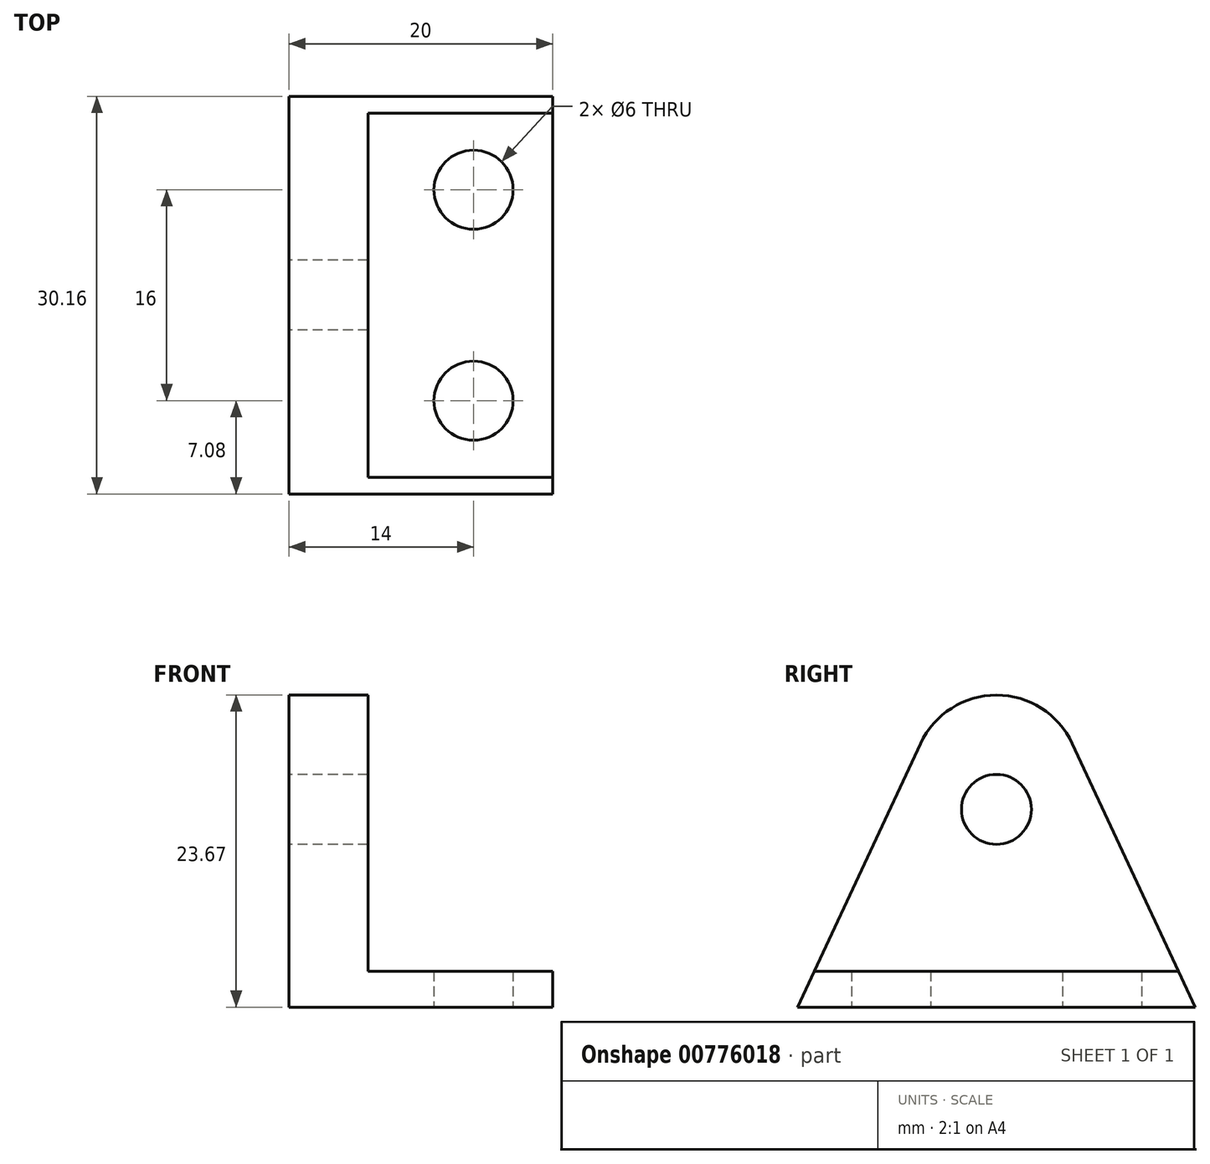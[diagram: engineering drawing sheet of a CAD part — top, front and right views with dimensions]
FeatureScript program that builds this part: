
annotation { "Feature Type Name" : "Feature", "Feature Type Description" : "" }
export const myFeature = defineFeature(function(context is Context, id is Id, definition is map)
    precondition{}
    {
        {
            var Q0;
            Q0=qCreatedBy(makeId("Right.planeOp"),FACE);
            var sketch = newSketch(context, id + "F0", { "sketchPlane" : qUnion([Q0])});
            skLineSegment(sketch, "E0", {"start": v(-15.08, 0) * mm, "end": v(-5.76, 20) * mm});
            skLineSegment(sketch, "E1", {"start": v(0, 32.34) * mm, "end": v(0, 0) * mm, "construction": true});
            skLineSegment(sketch, "E2", {"start": v(0, 0) * mm, "end": v(-15.08, 0) * mm});
            skLineSegment(sketch, "E3.MirrorCS", {"start": v(0, 0) * mm, "end": v(15.08, 0) * mm});
            skLineSegment(sketch, "E4.MirrorCS", {"start": v(15.08, 0) * mm, "end": v(5.76, 20) * mm});
            skCircle(sketch, "E5", {"center": v(0, 15) * mm, "radius": 2.65 * mm});
            skPoint(sketch, "E6.visualSharp", {"position": v(0, 32.34) * mm});
            skArc(sketch, "E6.filletArc", {"start": v(5.76, 20) * mm, "mid": v(0, 23.67) * mm, "end": v(-5.76, 20) * mm});
            skSolve(sketch);
        }
        {
            var Q0;
            Q0 = qSketchRegion(id + "F0", true);
            extrude(context, id + "F1", {"entities" : qUnion([Q0]), "depth" : 6 * mm, "offsetDistance" : 25.4 * mm});
        }
        {
            var Q0;
            Q0=qCreatedBy(makeId("Right.planeOp"),FACE);
            var sketch = newSketch(context, id + "F2", { "sketchPlane" : qUnion([Q0])});
            skLineSegment(sketch, "E7.bottom", {"start": v(-15.08, 0) * mm, "end": v(15.08, 0) * mm});
            skLineSegment(sketch, "E7.top", {"start": v(-13.81, 2.72) * mm, "end": v(13.81, 2.72) * mm});
            skLineSegment(sketch, "E7.left", {"start": v(-15.08, 0) * mm, "end": v(-13.81, 2.72) * mm});
            skLineSegment(sketch, "E7.right", {"start": v(15.08, 0) * mm, "end": v(13.81, 2.72) * mm});
            skSolve(sketch);
        }
        {
            var Q0;
            Q0 = qSketchRegion(id + "F2", true);
            extrude(context, id + "F3", {"entities" : qUnion([Q0]), "operationType" : NewBodyOperationType.ADD, "depth" : 20 * mm, "offsetDistance" : 25.4 * mm});
        }
        {
            var Q0;
            Q0=qCreatedBy(makeId("Top.planeOp"),FACE);
            var sketch = newSketch(context, id + "F4", { "sketchPlane" : qUnion([Q0])});
            skCircle(sketch, "E8", {"center": v(14, -8) * mm, "radius": 3 * mm});
            skLineSegment(sketch, "E9", {"start": v(0, 0) * mm, "end": v(27.47, 0) * mm, "construction": true});
            skCircle(sketch, "E10.MirrorC", {"center": v(14, 8) * mm, "radius": 3 * mm});
            skSolve(sketch);
        }
        {
            var Q0;
            Q0 = qSketchRegion(id + "F4", true);
            extrude(context, id + "F5", {"entities" : qUnion([Q0]), "operationType" : NewBodyOperationType.REMOVE, "depth" : 25.4 * mm, "offsetDistance" : 25.4 * mm});
        }
    });
